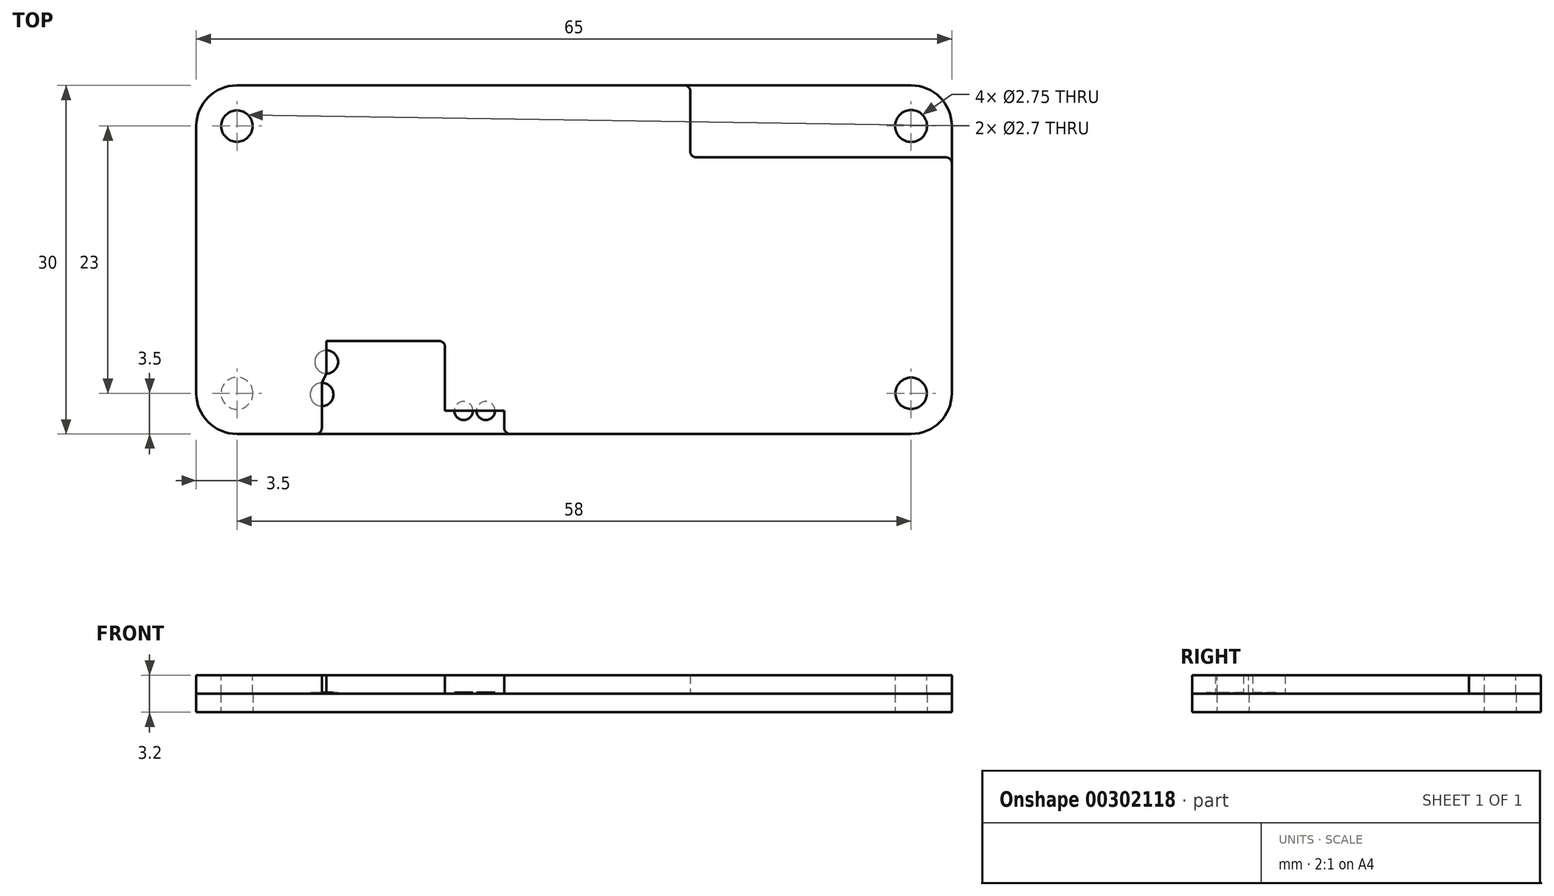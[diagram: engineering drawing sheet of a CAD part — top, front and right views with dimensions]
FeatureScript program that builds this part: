
annotation { "Feature Type Name" : "Feature", "Feature Type Description" : "" }
export const myFeature = defineFeature(function(context is Context, id is Id, definition is map)
    precondition{}
    {
        {
            var Q0;
            Q0=qCreatedBy(makeId("Top.planeOp"),FACE);
            var sketch = newSketch(context, id + "F0", { "sketchPlane" : qUnion([Q0])});
            skLineSegment(sketch, "E0.bottom", {"start": v(29, 15) * mm, "end": v(-29, 15) * mm});
            skLineSegment(sketch, "E0.top", {"start": v(29, -15) * mm, "end": v(-29, -15) * mm});
            skLineSegment(sketch, "E0.left", {"start": v(32.5, 11.5) * mm, "end": v(32.5, -11.5) * mm});
            skLineSegment(sketch, "E0.right", {"start": v(-32.5, 11.5) * mm, "end": v(-32.5, -11.5) * mm});
            skPoint(sketch, "E0.middle", {"position": v(0, 0) * mm});
            skPoint(sketch, "E1.visualSharp", {"position": v(-32.5, 15) * mm});
            skArc(sketch, "E1.filletArc", {"start": v(-29, 15) * mm, "mid": v(-31.47, 13.97) * mm, "end": v(-32.5, 11.5) * mm});
            skPoint(sketch, "E2.visualSharp", {"position": v(-32.5, -15) * mm});
            skArc(sketch, "E2.filletArc", {"start": v(-32.5, -11.5) * mm, "mid": v(-31.47, -13.97) * mm, "end": v(-29, -15) * mm});
            skPoint(sketch, "E3.visualSharp", {"position": v(32.5, -15) * mm});
            skArc(sketch, "E3.filletArc", {"start": v(29, -15) * mm, "mid": v(31.47, -13.97) * mm, "end": v(32.5, -11.5) * mm});
            skPoint(sketch, "E4.visualSharp", {"position": v(32.5, 15) * mm});
            skArc(sketch, "E4.filletArc", {"start": v(32.5, 11.5) * mm, "mid": v(31.47, 13.97) * mm, "end": v(29, 15) * mm});
            skCircle(sketch, "E5", {"center": v(-29, 11.5) * mm, "radius": 1.38 * mm});
            skCircle(sketch, "E6", {"center": v(-29, -11.5) * mm, "radius": 1.38 * mm});
            skCircle(sketch, "E7", {"center": v(29, -11.5) * mm, "radius": 1.38 * mm});
            skCircle(sketch, "E8", {"center": v(29, 11.5) * mm, "radius": 1.38 * mm});
            skSolve(sketch);
        }
        {
            var Q0;
            Q0=makeQuery(id+"F0.imprint","IMPRINT",FACE,{"disambiguationData":[TD([[makeQuery(id+"F0.imprint","IMPRINT",EDGE,{"derivedFrom":sQuery(id+"F0.wireOp",EDGE,"E0.bottom")}),1.0]])]});
            extrude(context, id + "F1", {"entities" : qUnion([Q0]), "depth" : 1.6 * mm});
        }
        {
            var Q0;
            Q0=makeQuery(id+"F1.opExtrude","CAP_FACE",FACE,{"disambiguationData":[OSD([sQuery(id+"F0.wireOp",EDGE,"E0.bottom"),sQuery(id+"F0.wireOp",EDGE,"E0.top"),sQuery(id+"F0.wireOp",EDGE,"E0.left"),sQuery(id+"F0.wireOp",EDGE,"E0.right"),sQuery(id+"F0.wireOp",EDGE,"E1.filletArc"),sQuery(id+"F0.wireOp",EDGE,"E2.filletArc"),sQuery(id+"F0.wireOp",EDGE,"E3.filletArc"),sQuery(id+"F0.wireOp",EDGE,"E4.filletArc"),sQuery(id+"F0.wireOp",EDGE,"E5"),sQuery(id+"F0.wireOp",EDGE,"E6"),sQuery(id+"F0.wireOp",EDGE,"E7"),sQuery(id+"F0.wireOp",EDGE,"E8"),sQuery(id+"F0.wireOp",EDGE,"NqQOvOVT-KunM-NpxJ-45oc-2Cs1jEsRzp99"),sQuery(id+"F0.wireOp",EDGE,"OkOPJhnL-l21R-TTLX-7vaQ-bLT5VOah6iPr"),sQuery(id+"F0.wireOp",EDGE,"8j5WUiNJ-V6kJ-tGhW-VHUZ-trNlVAVWzyD2"),sQuery(id+"F0.wireOp",EDGE,"yzwVbTsP-FCtw-uuZ8-G2hZ-PQp141aInich")])],"isStart":false});
            var sketch = newSketch(context, id + "F2", { "sketchPlane" : qUnion([Q0])});
            skPoint(sketch, "E9.middle", {"position": v(0, 0) * mm});
            skCircle(sketch, "E10", {"center": v(-21.7, -11.6) * mm, "radius": 1 * mm});
            skCircle(sketch, "E11", {"center": v(-21.3, -8.8) * mm, "radius": 1 * mm});
            skCircle(sketch, "E12", {"center": v(-9.5, -13) * mm, "radius": 0.8 * mm});
            skCircle(sketch, "E13", {"center": v(-7.6, -13) * mm, "radius": 0.8 * mm});
            skLineSegment(sketch, "E14", {"start": v(-21.3, -8.8) * mm, "end": v(-20.3, -8.8) * mm, "construction": true});
            skLineSegment(sketch, "E15", {"start": v(-21.3, -8.8) * mm, "end": v(-22.3, -8.8) * mm, "construction": true});
            skLineSegment(sketch, "E16", {"start": v(-21.3, -8.8) * mm, "end": v(-21.3, -7.8) * mm, "construction": true});
            skLineSegment(sketch, "E17", {"start": v(-21.3, -8.8) * mm, "end": v(-21.3, -9.8) * mm, "construction": true});
            skLineSegment(sketch, "E18", {"start": v(-21.7, -11.6) * mm, "end": v(-21.7, -10.6) * mm, "construction": true});
            skLineSegment(sketch, "E19", {"start": v(-21.7, -11.6) * mm, "end": v(-21.7, -12.6) * mm, "construction": true});
            skLineSegment(sketch, "E20", {"start": v(-21.7, -11.6) * mm, "end": v(-20.7, -11.6) * mm, "construction": true});
            skLineSegment(sketch, "E21", {"start": v(-21.7, -11.6) * mm, "end": v(-22.7, -11.6) * mm, "construction": true});
            skLineSegment(sketch, "E22", {"start": v(-9.5, -13) * mm, "end": v(-9.5, -13.8) * mm, "construction": true});
            skLineSegment(sketch, "E23", {"start": v(-9.5, -13) * mm, "end": v(-9.5, -12.2) * mm, "construction": true});
            skLineSegment(sketch, "E24", {"start": v(-9.5, -13) * mm, "end": v(-10.3, -13) * mm, "construction": true});
            skLineSegment(sketch, "E25", {"start": v(-9.5, -13) * mm, "end": v(-8.7, -13) * mm, "construction": true});
            skLineSegment(sketch, "E26", {"start": v(-7.6, -13) * mm, "end": v(-8.4, -13) * mm, "construction": true});
            skLineSegment(sketch, "E27", {"start": v(-7.6, -13) * mm, "end": v(-6.8, -13) * mm, "construction": true});
            skLineSegment(sketch, "E28", {"start": v(-7.6, -13) * mm, "end": v(-7.6, -13.8) * mm, "construction": true});
            skLineSegment(sketch, "E29", {"start": v(-7.6, -13) * mm, "end": v(-7.6, -12.2) * mm, "construction": true});
            skSolve(sketch);
        }
        {
            var Q0;
            Q0=makeQuery(id+"F2.imprint","IMPRINT",FACE,{"disambiguationData":[TD([[makeQuery(id+"F2.imprint","IMPRINT",EDGE,{"derivedFrom":sQuery(id+"F2.wireOp",EDGE,"E10")}),1.0]])]});
            var Q1;
            Q1=makeQuery(id+"F2.imprint","IMPRINT",FACE,{"disambiguationData":[TD([[makeQuery(id+"F2.imprint","IMPRINT",EDGE,{"derivedFrom":sQuery(id+"F2.wireOp",EDGE,"E11")}),1.0]])]});
            var Q2;
            Q2=makeQuery(id+"F2.imprint","IMPRINT",FACE,{"disambiguationData":[TD([[makeQuery(id+"F2.imprint","IMPRINT",EDGE,{"derivedFrom":sQuery(id+"F2.wireOp",EDGE,"E12")}),1.0]])]});
            var Q3;
            Q3=makeQuery(id+"F2.imprint","IMPRINT",FACE,{"disambiguationData":[TD([[makeQuery(id+"F2.imprint","IMPRINT",EDGE,{"derivedFrom":sQuery(id+"F2.wireOp",EDGE,"E13")}),1.0]])]});
            extrude(context, id + "F3", {"entities" : qUnion([Q0, Q1, Q2, Q3]), "operationType" : NewBodyOperationType.ADD, "depth" : 0.1 * mm});
        }
        {
            var Q0;
            Q0=makeQuery(id+"F1.opExtrude","CAP_FACE",FACE,{"disambiguationData":[OSD([sQuery(id+"F0.wireOp",EDGE,"E0.bottom"),sQuery(id+"F0.wireOp",EDGE,"E0.top"),sQuery(id+"F0.wireOp",EDGE,"E0.left"),sQuery(id+"F0.wireOp",EDGE,"E0.right"),sQuery(id+"F0.wireOp",EDGE,"E1.filletArc"),sQuery(id+"F0.wireOp",EDGE,"E2.filletArc"),sQuery(id+"F0.wireOp",EDGE,"E3.filletArc"),sQuery(id+"F0.wireOp",EDGE,"E4.filletArc"),sQuery(id+"F0.wireOp",EDGE,"E5"),sQuery(id+"F0.wireOp",EDGE,"E6"),sQuery(id+"F0.wireOp",EDGE,"E7"),sQuery(id+"F0.wireOp",EDGE,"E8")])],"isStart":false});
            var sketch = newSketch(context, id + "F4", { "sketchPlane" : qUnion([Q0])});
            skLineSegment(sketch, "E30.bottom", {"start": v(9.5, 15) * mm, "end": v(-29, 15) * mm});
            skLineSegment(sketch, "E30.top", {"start": v(29, -15) * mm, "end": v(-5.5, -15) * mm});
            skLineSegment(sketch, "E30.left", {"start": v(32.5, 8.3) * mm, "end": v(32.5, -11.5) * mm});
            skLineSegment(sketch, "E30.right", {"start": v(-32.5, 11.5) * mm, "end": v(-32.5, -11.5) * mm});
            skPoint(sketch, "E30.middle", {"position": v(0, 0) * mm});
            skPoint(sketch, "E31.visualSharp", {"position": v(-32.5, 15) * mm});
            skArc(sketch, "E31.filletArc", {"start": v(-29, 15) * mm, "mid": v(-31.47, 13.97) * mm, "end": v(-32.5, 11.5) * mm});
            skPoint(sketch, "E32.visualSharp", {"position": v(-32.5, -15) * mm});
            skArc(sketch, "E32.filletArc", {"start": v(-32.5, -11.5) * mm, "mid": v(-31.47, -13.97) * mm, "end": v(-29, -15) * mm});
            skPoint(sketch, "E33.visualSharp", {"position": v(32.5, -15) * mm});
            skArc(sketch, "E33.filletArc", {"start": v(29, -15) * mm, "mid": v(31.47, -13.97) * mm, "end": v(32.5, -11.5) * mm});
            skPoint(sketch, "E34.visualSharp", {"position": v(32.5, 15) * mm});
            skLineSegment(sketch, "E35.trimOffspring", {"start": v(-22.2, -15) * mm, "end": v(-29, -15) * mm});
            skLineSegment(sketch, "E36", {"start": v(10, 14.5) * mm, "end": v(10, 9.3) * mm});
            skLineSegment(sketch, "E37", {"start": v(10.5, 8.8) * mm, "end": v(32, 8.8) * mm});
            skLineSegment(sketch, "E38", {"start": v(-21.7, -10.6) * mm, "end": v(-21.7, -14.5) * mm});
            skLineSegment(sketch, "E39", {"start": v(-7.6, -13) * mm, "end": v(-9.5, -13) * mm});
            skLineSegment(sketch, "E40", {"start": v(-21.3, -9.8) * mm, "end": v(-21.7, -10.6) * mm});
            skLineSegment(sketch, "E41", {"start": v(-21.3, -7.8) * mm, "end": v(-21.3, -7) * mm});
            skLineSegment(sketch, "E42", {"start": v(-9.5, -13) * mm, "end": v(-11.1, -13) * mm});
            skLineSegment(sketch, "E43", {"start": v(-11.1, -13) * mm, "end": v(-11.1, -7.5) * mm});
            skLineSegment(sketch, "E44", {"start": v(-11.6, -7) * mm, "end": v(-21.3, -7) * mm});
            skLineSegment(sketch, "E45", {"start": v(-7.6, -13) * mm, "end": v(-6, -13) * mm});
            skLineSegment(sketch, "E46", {"start": v(-6, -13) * mm, "end": v(-6, -14.5) * mm});
            skPoint(sketch, "E47.visualSharp", {"position": v(-11.1, -7) * mm});
            skArc(sketch, "E47.filletArc", {"start": v(-11.1, -7.5) * mm, "mid": v(-11.25, -7.15) * mm, "end": v(-11.6, -7) * mm});
            skPoint(sketch, "E48.visualSharp", {"position": v(-21.7, -15) * mm});
            skArc(sketch, "E48.filletArc", {"start": v(-22.2, -15) * mm, "mid": v(-21.85, -14.85) * mm, "end": v(-21.7, -14.5) * mm});
            skPoint(sketch, "E49.visualSharp", {"position": v(-6, -15) * mm});
            skArc(sketch, "E49.filletArc", {"start": v(-6, -14.5) * mm, "mid": v(-5.85, -14.85) * mm, "end": v(-5.5, -15) * mm});
            skPoint(sketch, "E50.visualSharp", {"position": v(10, 8.8) * mm});
            skArc(sketch, "E50.filletArc", {"start": v(10, 9.3) * mm, "mid": v(10.15, 8.95) * mm, "end": v(10.5, 8.8) * mm});
            skPoint(sketch, "E51.visualSharp", {"position": v(32.5, 8.8) * mm});
            skArc(sketch, "E51.filletArc", {"start": v(32.5, 8.3) * mm, "mid": v(32.35, 8.65) * mm, "end": v(32, 8.8) * mm});
            skPoint(sketch, "E52.visualSharp", {"position": v(10, 15) * mm});
            skArc(sketch, "E52.filletArc", {"start": v(10, 14.5) * mm, "mid": v(9.85, 14.85) * mm, "end": v(9.5, 15) * mm});
            skLineSegment(sketch, "E53", {"start": v(-21.3, -7.8) * mm, "end": v(-21.3, -9.8) * mm});
            skSolve(sketch);
        }
        {
            var Q0;
            Q0 = qSketchRegion(id + "F4", true);
            extrude(context, id + "F5", {"entities" : qUnion([Q0]), "depth" : 1.6 * mm});
        }
        {
            var Q0;
            Q0=makeQuery(id+"F5.opExtrude","CAP_FACE",FACE,{"disambiguationData":[OSD([sQuery(id+"F4.wireOp",EDGE,"E30.bottom"),sQuery(id+"F4.wireOp",EDGE,"E30.top"),sQuery(id+"F4.wireOp",EDGE,"E30.left"),sQuery(id+"F4.wireOp",EDGE,"E30.right"),sQuery(id+"F4.wireOp",EDGE,"E31.filletArc"),sQuery(id+"F4.wireOp",EDGE,"E32.filletArc"),sQuery(id+"F4.wireOp",EDGE,"E33.filletArc"),sQuery(id+"F4.wireOp",EDGE,"E35.trimOffspring"),sQuery(id+"F4.wireOp",EDGE,"E36"),sQuery(id+"F4.wireOp",EDGE,"E37"),sQuery(id+"F4.wireOp",EDGE,"E38"),sQuery(id+"F4.wireOp",EDGE,"E39"),sQuery(id+"F4.wireOp",EDGE,"E40"),sQuery(id+"F4.wireOp",EDGE,"E41"),sQuery(id+"F4.wireOp",EDGE,"E42"),sQuery(id+"F4.wireOp",EDGE,"E43"),sQuery(id+"F4.wireOp",EDGE,"E44"),sQuery(id+"F4.wireOp",EDGE,"E45"),sQuery(id+"F4.wireOp",EDGE,"E46"),sQuery(id+"F4.wireOp",EDGE,"E47.filletArc"),sQuery(id+"F4.wireOp",EDGE,"E48.filletArc"),sQuery(id+"F4.wireOp",EDGE,"E49.filletArc"),sQuery(id+"F4.wireOp",EDGE,"E50.filletArc"),sQuery(id+"F4.wireOp",EDGE,"E51.filletArc"),sQuery(id+"F4.wireOp",EDGE,"E52.filletArc"),sQuery(id+"F4.wireOp",EDGE,"E53")])],"isStart":false});
            var sketch = newSketch(context, id + "F6", { "sketchPlane" : qUnion([Q0])});
            skPoint(sketch, "E54", {"position": v(27.7, 4.42) * mm});
            skPoint(sketch, "E55", {"position": v(-0.23, -11.18) * mm});
            skCircle(sketch, "E56", {"center": v(-29, 11.5) * mm, "radius": 1.35 * mm});
            skCircle(sketch, "E57", {"center": v(29, -11.5) * mm, "radius": 1.35 * mm});
            skSolve(sketch);
        }
        {
            var Q0;
            Q0=makeQuery(id+"F1.opExtrude","CAP_FACE",FACE,{"disambiguationData":[OSD([sQuery(id+"F0.wireOp",EDGE,"E0.bottom"),sQuery(id+"F0.wireOp",EDGE,"E0.top"),sQuery(id+"F0.wireOp",EDGE,"E0.left"),sQuery(id+"F0.wireOp",EDGE,"E0.right"),sQuery(id+"F0.wireOp",EDGE,"E1.filletArc"),sQuery(id+"F0.wireOp",EDGE,"E2.filletArc"),sQuery(id+"F0.wireOp",EDGE,"E3.filletArc"),sQuery(id+"F0.wireOp",EDGE,"E4.filletArc"),sQuery(id+"F0.wireOp",EDGE,"E5"),sQuery(id+"F0.wireOp",EDGE,"E6"),sQuery(id+"F0.wireOp",EDGE,"E7"),sQuery(id+"F0.wireOp",EDGE,"E8")])],"isStart":true});
            var sketch = newSketch(context, id + "F7", { "sketchPlane" : qUnion([Q0])});
            skPoint(sketch, "E58", {"position": v(-27.7, -5.25) * mm});
            skPoint(sketch, "E59", {"position": v(-25, 13.75) * mm});
            skPoint(sketch, "E60", {"position": v(-12, 13.75) * mm});
            skSolve(sketch);
        }
        {
            var Q0;
            Q0=makeQuery(id+"F6.imprint","IMPRINT",FACE,{"disambiguationData":[TD([[makeQuery(id+"F6.imprint","IMPRINT",EDGE,{"derivedFrom":sQuery(id+"F6.wireOp",EDGE,"E56")}),1.0]])]});
            var Q1;
            Q1=makeQuery(id+"F6.imprint","IMPRINT",FACE,{"disambiguationData":[TD([[makeQuery(id+"F6.imprint","IMPRINT",EDGE,{"derivedFrom":sQuery(id+"F6.wireOp",EDGE,"E57")}),1.0]])]});
            extrude(context, id + "F8", {"entities" : qUnion([Q0, Q1]), "operationType" : NewBodyOperationType.REMOVE, "oppositeDirection" : true, "depth" : 1.6 * mm});
        }
    });
